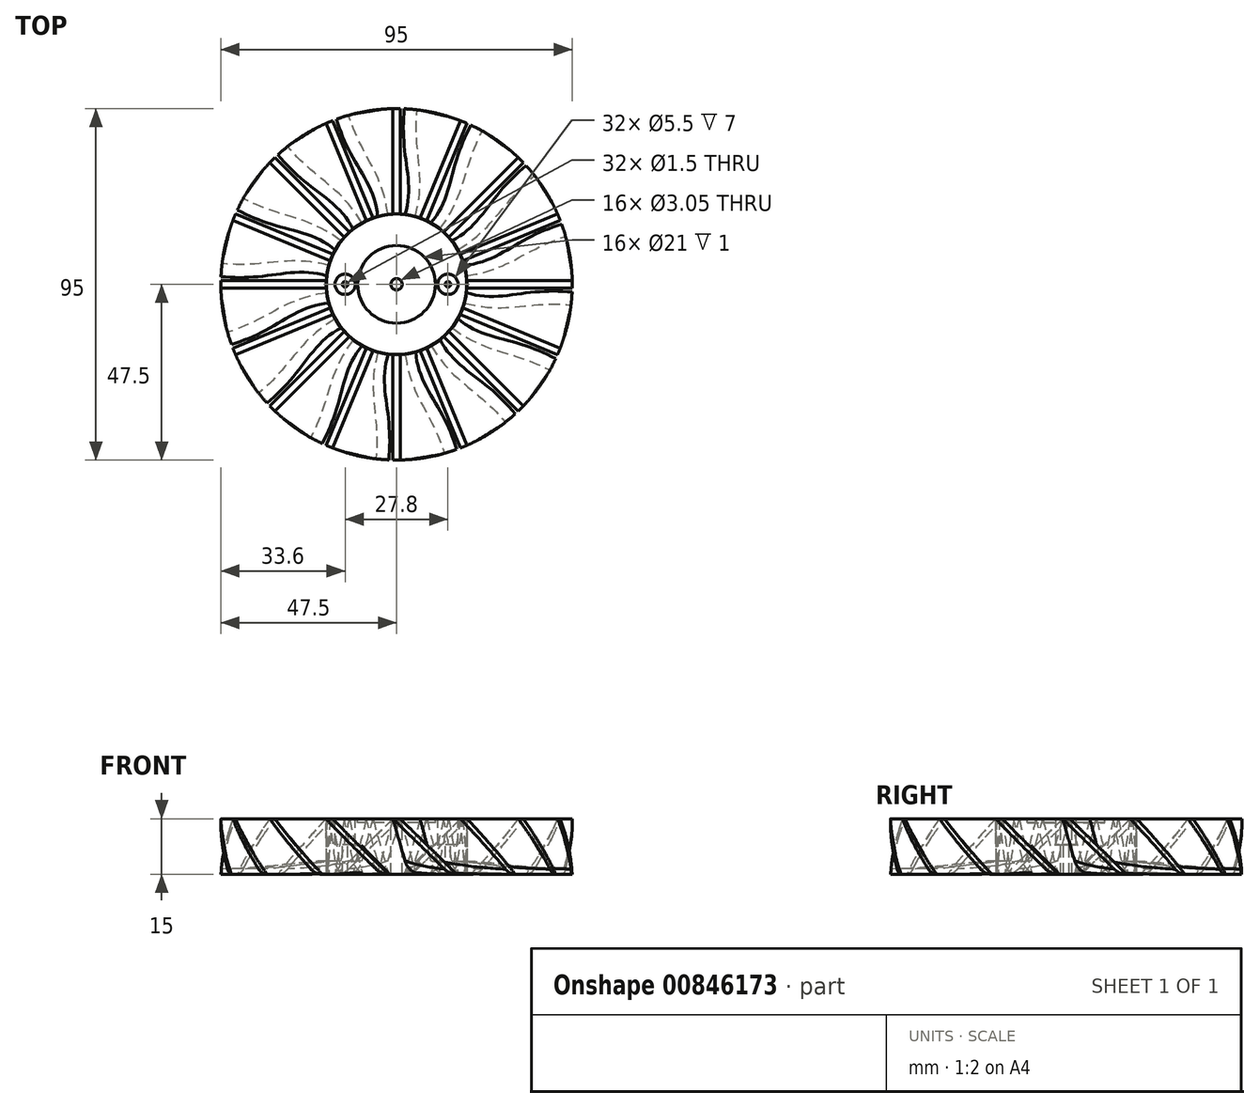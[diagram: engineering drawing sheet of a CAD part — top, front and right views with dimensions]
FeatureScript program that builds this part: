
annotation { "Feature Type Name" : "Feature", "Feature Type Description" : "" }
export const myFeature = defineFeature(function(context is Context, id is Id, definition is map)
    precondition{}
    {
        {
            var Q0;
            Q0=qCreatedBy(makeId("Top.planeOp"),FACE);
            var sketch = newSketch(context, id + "F0", { "sketchPlane" : qUnion([Q0])});
            skCircle(sketch, "E0", {"center": v(0, 0) * mm, "radius": 19 * mm});
            skSolve(sketch);
        }
        {
            var Q0;
            Q0=qSketchRegion(id+"F0",true);
            extrude(context, id + "F1", {"entities" : qUnion([Q0]), "depth" : 15 * mm, "offsetDistance" : 25 * mm});
        }
        {
            var Q0;
            Q0=makeQuery(id+"F1.opExtrude","CAP_FACE",FACE,{"disambiguationData":[OSD([sQuery(id+"F0.wireOp",EDGE,"E0")])],"isStart":true});
            var sketch = newSketch(context, id + "F2", { "sketchPlane" : qUnion([Q0])});
            skLineSegment(sketch, "E1", {"start": v(0, 0) * mm, "end": v(-3.3, -18.71) * mm});
            skLineSegment(sketch, "E2", {"start": v(0, 0) * mm, "end": v(0, -19) * mm, "construction": true});
            skCircle(sketch, "E3", {"center": v(0, 0) * mm, "radius": 49 * mm, "construction": true});
            skFitSpline(sketch, "E4", {"points": [v(-3.3, -18.71) * mm, v(-14.76, -46.73) * mm], "startDerivative": vector(-6.25, -35.44) * mm, "endDerivative": vector(-12.11, -41.2) * mm});
            skFitSpline(sketch, "E5.0", {"points": [v(-5.27, -18.36) * mm, v(-5.52, -19.77) * mm, v(-6.1, -22.3) * mm, v(-7.22, -25.45) * mm, v(-8.53, -28.26) * mm, v(-10.02, -31) * mm, v(-11.66, -33.93) * mm, v(-13.37, -37.26) * mm, v(-15.07, -41.21) * mm, v(-16.15, -44.4) * mm, v(-16.67, -46.16) * mm]});
            skLineSegment(sketch, "E5.1", {"start": v(-1.97, 0.35) * mm, "end": v(-5.27, -18.36) * mm});
            skLineSegment(sketch, "E6", {"start": v(-14.76, -46.73) * mm, "end": v(-16.67, -46.16) * mm});
            skLineSegment(sketch, "E7", {"start": v(-3.3, -18.71) * mm, "end": v(-4.64, -17.92) * mm});
            skLineSegment(sketch, "E8", {"start": v(-4.64, -17.92) * mm, "end": v(-5.2, -17.92) * mm});
            skLineSegment(sketch, "E9", {"start": v(-5.2, -17.92) * mm, "end": v(-5.27, -18.36) * mm});
            skSolve(sketch);
        }
        {
            var Q0;
            Q0=makeQuery(id+"F1.opExtrude","CAP_FACE",FACE,{"disambiguationData":[OSD([sQuery(id+"F0.wireOp",EDGE,"E0")])],"isStart":false});
            var sketch = newSketch(context, id + "F3", { "sketchPlane" : qUnion([Q0])});
            skLineSegment(sketch, "E10", {"start": v(-0.97, 18.98) * mm, "end": v(0.97, 18.98) * mm});
            skLineSegment(sketch, "E11", {"start": v(0.97, 18.98) * mm, "end": v(0.97, 49) * mm});
            skLineSegment(sketch, "E12", {"start": v(0.97, 49) * mm, "end": v(-0.97, 49) * mm});
            skLineSegment(sketch, "E13", {"start": v(-0.97, 49) * mm, "end": v(-0.97, 18.98) * mm});
            skSolve(sketch);
        }
        {
            var Q1;
            {var subQ4=sQuery(id+"F2.wireOp",EDGE,"E4");Q1=makeQuery(id+"F2.imprint","IMPRINT",FACE,{"disambiguationData":[TD([[makeQuery(id+"F2.imprint","IMPRINT",EDGE,{"derivedFrom":subQ4}),-1.0]])]});}
            var Q2;
            {var subQ0=sQuery(id+"F3.wireOp",EDGE,"E11");Q2=makeQuery(id+"F3.imprint","IMPRINT",FACE,{"disambiguationData":[TD([[makeQuery(id+"F3.imprint","IMPRINT",EDGE,{"derivedFrom":subQ0}),1.0]])]});}
            var Q3;
            Q3=sQuery(id+"F2.wireOp",VERTEX,"E6.end");
            var Q4;
            Q4=sQuery(id+"F3.wireOp",VERTEX,"E13.start");
            loft(context, id + "F4", {"operationType" : NewBodyOperationType.ADD, "sheetProfilesArray" : [{ "sheetProfileEntities" : qUnion([Q1]) }, { "sheetProfileEntities" : qUnion([Q2]) }], "matchConnections" : true, "connections" : [{ "connectionEntities" : qUnion([Q3, Q4]), "connectionEdgeQueries" : qUnion([]), "connectionEdgeParameters" : [] }]});
        }
        {
            var Q0;
            Q0=makeQuery(id+"F4.opLoft","SWEPT_EDGE",EDGE,{"disambiguationData":[OSD([sQuery(id+"F2.wireOp",EDGE,"E4"),sQuery(id+"F2.wireOp",EDGE,"E6"),sQuery(id+"F3.wireOp",EDGE,"E11"),sQuery(id+"F3.wireOp",EDGE,"E12")])]});
            var Q1;
            Q1=makeQuery(id+"F4.opLoft","SWEPT_EDGE",EDGE,{"disambiguationData":[OSD([sQuery(id+"F2.wireOp",EDGE,"E5.0"),sQuery(id+"F2.wireOp",EDGE,"E6"),sQuery(id+"F3.wireOp",EDGE,"E12"),sQuery(id+"F3.wireOp",EDGE,"E13")])]});
            fillet(context, id + "F5", {"entities" : qUnion([Q0, Q1]), "radius" : 1 * mm, "tangentPropagation" : true, "allowEdgeOverflow" : false});
        }
        {
            var Q0;
            Q0=qCreatedBy(makeId("Right.planeOp"),FACE);
            var sketch = newSketch(context, id + "F6", { "sketchPlane" : qUnion([Q0])});
            skLineSegment(sketch, "E14", {"start": v(0, -43.46) * mm, "end": v(0, 53.88) * mm, "construction": true});
            skSolve(sketch);
        }
        {
            var Q0;
            Q0=makeQuery(id+"F1.opExtrude","SWEPT_BODY",BODY,{"disambiguationData":[OSD([sQuery(id+"F0.wireOp",EDGE,"E0")])]});
            var Q1;
            Q1=sQuery(id+"F6.wireOp",EDGE,"E14");
            circularPattern(context, id + "F7", {"entities" : qUnion([Q0]), "axis" : qUnion([Q1]), "angle" : 360 * degree, "instanceCount" : 16, "equalSpace" : true});
        }
        {
            var Q0;
            {var subQ0=sQuery(id+"F3.wireOp",EDGE,"E11");var subQ3=sQuery(id+"F0.wireOp",EDGE,"E0");Q0=makeQuery(id+"F7.opPattern","COPY",FACE,{"derivedFrom":makeQuery(id+"F4.boolean.opBoolean","MERGE",FACE,{"derivedFrom":[makeQuery(id+"F1.opExtrude","CAP_FACE",FACE,{"disambiguationData":[OSD([subQ3])],"isStart":false}),makeQuery(id+"F4.opLoft","CAP_FACE",FACE,{"disambiguationData":[OSD([makeQuery(id+"F3.imprint","IMPRINT",FACE,{"disambiguationData":[TD([[makeQuery(id+"F3.imprint","IMPRINT",EDGE,{"derivedFrom":subQ0}),1.0]])]})])],"isStart":true})]}),"instanceName":"2"});}
            var sketch = newSketch(context, id + "F8", { "sketchPlane" : qUnion([Q0])});
            skCircle(sketch, "E15", {"center": v(0, 0) * mm, "radius": 47.5 * mm});
            skCircle(sketch, "E16", {"center": v(0, 0) * mm, "radius": 52.62 * mm});
            skSolve(sketch);
        }
        {
            var Q0;
            Q0=qSketchRegion(id+"F8",true);
            extrude(context, id + "F9", {"entities" : qUnion([Q0]), "operationType" : NewBodyOperationType.REMOVE, "endBound" : BoundingType.THROUGH_ALL, "oppositeDirection" : true, "depth" : 15 * mm, "offsetDistance" : 25 * mm});
        }
        {
            var Q0;
            {var subQ0=sQuery(id+"F3.wireOp",EDGE,"E11");var subQ3=sQuery(id+"F0.wireOp",EDGE,"E0");Q0=makeQuery(id+"F7.opPattern","COPY",FACE,{"derivedFrom":makeQuery(id+"F4.boolean.opBoolean","MERGE",FACE,{"derivedFrom":[makeQuery(id+"F1.opExtrude","CAP_FACE",FACE,{"disambiguationData":[OSD([subQ3])],"isStart":false}),makeQuery(id+"F4.opLoft","CAP_FACE",FACE,{"disambiguationData":[OSD([makeQuery(id+"F3.imprint","IMPRINT",FACE,{"disambiguationData":[TD([[makeQuery(id+"F3.imprint","IMPRINT",EDGE,{"derivedFrom":subQ0}),1.0]])]})])],"isStart":true})]}),"instanceName":"11"});}
            var sketch = newSketch(context, id + "F10", { "sketchPlane" : qUnion([Q0])});
            skCircle(sketch, "E17", {"center": v(0, 0) * mm, "radius": 1.52 * mm});
            skSolve(sketch);
        }
        {
            var Q0;
            Q0=qSketchRegion(id+"F10",true);
            extrude(context, id + "F11", {"entities" : qUnion([Q0]), "operationType" : NewBodyOperationType.REMOVE, "endBound" : BoundingType.THROUGH_ALL, "oppositeDirection" : true, "depth" : 25 * mm, "offsetDistance" : 25 * mm});
        }
        {
            var Q0;
            {var subQ0=sQuery(id+"F3.wireOp",EDGE,"E11");var subQ3=sQuery(id+"F0.wireOp",EDGE,"E0");Q0=makeQuery(id+"F7.opPattern","COPY",FACE,{"derivedFrom":makeQuery(id+"F4.boolean.opBoolean","MERGE",FACE,{"derivedFrom":[makeQuery(id+"F1.opExtrude","CAP_FACE",FACE,{"disambiguationData":[OSD([subQ3])],"isStart":false}),makeQuery(id+"F4.opLoft","CAP_FACE",FACE,{"disambiguationData":[OSD([makeQuery(id+"F3.imprint","IMPRINT",FACE,{"disambiguationData":[TD([[makeQuery(id+"F3.imprint","IMPRINT",EDGE,{"derivedFrom":subQ0}),1.0]])]})])],"isStart":true})]}),"instanceName":"8"});}
            var sketch = newSketch(context, id + "F12", { "sketchPlane" : qUnion([Q0])});
            skLineSegment(sketch, "E18", {"start": v(0, 0) * mm, "end": v(14.1, 0) * mm, "construction": true});
            skLineSegment(sketch, "E19", {"start": v(14.1, 0) * mm, "end": v(-16.8, 0) * mm, "construction": true});
            skCircle(sketch, "E20", {"center": v(-13.9, 0) * mm, "radius": 2.75 * mm});
            skCircle(sketch, "E21", {"center": v(13.9, 0) * mm, "radius": 2.75 * mm});
            skPoint(sketch, "E22", {"position": v(-11.15, 0) * mm});
            skPoint(sketch, "E23", {"position": v(11.15, 0) * mm});
            skCircle(sketch, "E24", {"center": v(0, 0) * mm, "radius": 10.5 * mm});
            skSolve(sketch);
        }
        {
            var Q0;
            Q0=makeQuery(id+"F12.imprint","IMPRINT",FACE,{"disambiguationData":[TD([[makeQuery(id+"F12.imprint","IMPRINT",EDGE,{"derivedFrom":sQuery(id+"F12.wireOp",EDGE,"E24")}),1.0]])]});
            extrude(context, id + "F13", {"entities" : qUnion([Q0]), "operationType" : NewBodyOperationType.REMOVE, "oppositeDirection" : true, "depth" : 1 * mm, "offsetDistance" : 25 * mm});
        }
        {
            var Q0;
            Q0=makeQuery(id+"F12.imprint","IMPRINT",FACE,{"disambiguationData":[TD([[makeQuery(id+"F12.imprint","IMPRINT",EDGE,{"derivedFrom":sQuery(id+"F12.wireOp",EDGE,"E20")}),1.0]])]});
            var Q1;
            Q1=makeQuery(id+"F12.imprint","IMPRINT",FACE,{"disambiguationData":[TD([[makeQuery(id+"F12.imprint","IMPRINT",EDGE,{"derivedFrom":sQuery(id+"F12.wireOp",EDGE,"E21")}),1.0]])]});
            extrude(context, id + "F14", {"entities" : qUnion([Q0, Q1]), "operationType" : NewBodyOperationType.REMOVE, "oppositeDirection" : true, "depth" : 7 * mm, "offsetDistance" : 25 * mm});
        }
        {
            var Q0;
            Q0=makeQuery(id+"F14.boolean.opBoolean","COPY",FACE,{"disambiguationData":[OD(2.0)],"derivedFrom":makeQuery(id+"F14.opExtrude","CAP_FACE",FACE,{"disambiguationData":[OSD([sQuery(id+"F12.wireOp",EDGE,"E20")])],"isStart":false})});
            var sketch = newSketch(context, id + "F15", { "sketchPlane" : qUnion([Q0])});
            skCircle(sketch, "E25", {"center": v(-13.9, 0) * mm, "radius": 0.75 * mm});
            skSolve(sketch);
        }
        {
            var Q0;
            Q0=qSketchRegion(id+"F15",true);
            extrude(context, id + "F16", {"entities" : qUnion([Q0]), "operationType" : NewBodyOperationType.REMOVE, "oppositeDirection" : true, "depth" : 25 * mm, "offsetDistance" : 25 * mm});
        }
        {
            var Q0;
            Q0=makeQuery(id+"F14.boolean.opBoolean","COPY",FACE,{"disambiguationData":[OD(2.0)],"derivedFrom":makeQuery(id+"F14.opExtrude","CAP_FACE",FACE,{"disambiguationData":[OSD([sQuery(id+"F12.wireOp",EDGE,"E21")])],"isStart":false})});
            var sketch = newSketch(context, id + "F17", { "sketchPlane" : qUnion([Q0])});
            skCircle(sketch, "E26", {"center": v(13.9, 0) * mm, "radius": 0.75 * mm});
            skSolve(sketch);
        }
        {
            var Q0;
            Q0=qSketchRegion(id+"F17",true);
            extrude(context, id + "F18", {"entities" : qUnion([Q0]), "operationType" : NewBodyOperationType.REMOVE, "oppositeDirection" : true, "depth" : 25 * mm, "offsetDistance" : 25 * mm});
        }
        {
            var Q0;
            Q0=makeQuery(id+"F7.opPattern","COPY",EDGE,{"derivedFrom":makeQuery(id+"F4.opLoft","MID_CAP_EDGE",EDGE,{"disambiguationData":[OSD([sQuery(id+"F0.wireOp",EDGE,"E0"),sQuery(id+"F2.wireOp",EDGE,"E4"),sQuery(id+"F2.wireOp",EDGE,"E6"),sQuery(id+"F2.wireOp",EDGE,"E7")])],"capPos":0.0}),"instanceName":"10"});
            var Q1;
            Q1=makeQuery(id+"F7.opPattern","COPY",EDGE,{"derivedFrom":makeQuery(id+"F4.opLoft","MID_CAP_EDGE",EDGE,{"disambiguationData":[OSD([sQuery(id+"F0.wireOp",EDGE,"E0"),sQuery(id+"F2.wireOp",EDGE,"E4"),sQuery(id+"F2.wireOp",EDGE,"E6"),sQuery(id+"F2.wireOp",EDGE,"E7")])],"capPos":0.0}),"instanceName":"11"});
            var Q2;
            Q2=makeQuery(id+"F7.opPattern","COPY",EDGE,{"derivedFrom":makeQuery(id+"F4.opLoft","MID_CAP_EDGE",EDGE,{"disambiguationData":[OSD([sQuery(id+"F0.wireOp",EDGE,"E0"),sQuery(id+"F2.wireOp",EDGE,"E4"),sQuery(id+"F2.wireOp",EDGE,"E6"),sQuery(id+"F2.wireOp",EDGE,"E7")])],"capPos":0.0}),"instanceName":"12"});
            var Q3;
            Q3=makeQuery(id+"F7.opPattern","COPY",EDGE,{"derivedFrom":makeQuery(id+"F4.opLoft","MID_CAP_EDGE",EDGE,{"disambiguationData":[OSD([sQuery(id+"F0.wireOp",EDGE,"E0"),sQuery(id+"F2.wireOp",EDGE,"E4"),sQuery(id+"F2.wireOp",EDGE,"E6"),sQuery(id+"F2.wireOp",EDGE,"E7")])],"capPos":0.0}),"instanceName":"13"});
            var Q4;
            Q4=makeQuery(id+"F7.opPattern","COPY",EDGE,{"derivedFrom":makeQuery(id+"F4.opLoft","MID_CAP_EDGE",EDGE,{"disambiguationData":[OSD([sQuery(id+"F0.wireOp",EDGE,"E0"),sQuery(id+"F2.wireOp",EDGE,"E4"),sQuery(id+"F2.wireOp",EDGE,"E6"),sQuery(id+"F2.wireOp",EDGE,"E7")])],"capPos":0.0}),"instanceName":"14"});
            var Q5;
            Q5=makeQuery(id+"F7.opPattern","COPY",EDGE,{"derivedFrom":makeQuery(id+"F4.opLoft","MID_CAP_EDGE",EDGE,{"disambiguationData":[OSD([sQuery(id+"F0.wireOp",EDGE,"E0"),sQuery(id+"F2.wireOp",EDGE,"E4"),sQuery(id+"F2.wireOp",EDGE,"E6"),sQuery(id+"F2.wireOp",EDGE,"E7")])],"capPos":0.0}),"instanceName":"15"});
            var Q6;
            Q6=makeQuery(id+"F4.opLoft","MID_CAP_EDGE",EDGE,{"disambiguationData":[OSD([sQuery(id+"F0.wireOp",EDGE,"E0"),sQuery(id+"F2.wireOp",EDGE,"E4"),sQuery(id+"F2.wireOp",EDGE,"E6"),sQuery(id+"F2.wireOp",EDGE,"E7")])],"capPos":0.0});
            var Q7;
            Q7=makeQuery(id+"F7.opPattern","COPY",EDGE,{"derivedFrom":makeQuery(id+"F4.opLoft","MID_CAP_EDGE",EDGE,{"disambiguationData":[OSD([sQuery(id+"F0.wireOp",EDGE,"E0"),sQuery(id+"F2.wireOp",EDGE,"E4"),sQuery(id+"F2.wireOp",EDGE,"E6"),sQuery(id+"F2.wireOp",EDGE,"E7")])],"capPos":0.0}),"instanceName":"1"});
            var Q8;
            Q8=makeQuery(id+"F7.opPattern","COPY",EDGE,{"derivedFrom":makeQuery(id+"F4.opLoft","MID_CAP_EDGE",EDGE,{"disambiguationData":[OSD([sQuery(id+"F0.wireOp",EDGE,"E0"),sQuery(id+"F2.wireOp",EDGE,"E4"),sQuery(id+"F2.wireOp",EDGE,"E6"),sQuery(id+"F2.wireOp",EDGE,"E7")])],"capPos":0.0}),"instanceName":"2"});
            var Q9;
            Q9=makeQuery(id+"F7.opPattern","COPY",EDGE,{"derivedFrom":makeQuery(id+"F4.opLoft","MID_CAP_EDGE",EDGE,{"disambiguationData":[OSD([sQuery(id+"F0.wireOp",EDGE,"E0"),sQuery(id+"F2.wireOp",EDGE,"E4"),sQuery(id+"F2.wireOp",EDGE,"E6"),sQuery(id+"F2.wireOp",EDGE,"E7")])],"capPos":0.0}),"instanceName":"3"});
            var Q10;
            Q10=makeQuery(id+"F7.opPattern","COPY",EDGE,{"derivedFrom":makeQuery(id+"F4.opLoft","MID_CAP_EDGE",EDGE,{"disambiguationData":[OSD([sQuery(id+"F0.wireOp",EDGE,"E0"),sQuery(id+"F2.wireOp",EDGE,"E4"),sQuery(id+"F2.wireOp",EDGE,"E6"),sQuery(id+"F2.wireOp",EDGE,"E7")])],"capPos":0.0}),"instanceName":"4"});
            var Q11;
            Q11=makeQuery(id+"F7.opPattern","COPY",EDGE,{"derivedFrom":makeQuery(id+"F4.opLoft","MID_CAP_EDGE",EDGE,{"disambiguationData":[OSD([sQuery(id+"F0.wireOp",EDGE,"E0"),sQuery(id+"F2.wireOp",EDGE,"E4"),sQuery(id+"F2.wireOp",EDGE,"E6"),sQuery(id+"F2.wireOp",EDGE,"E7")])],"capPos":0.0}),"instanceName":"5"});
            var Q12;
            Q12=makeQuery(id+"F7.opPattern","COPY",EDGE,{"derivedFrom":makeQuery(id+"F4.opLoft","MID_CAP_EDGE",EDGE,{"disambiguationData":[OSD([sQuery(id+"F0.wireOp",EDGE,"E0"),sQuery(id+"F2.wireOp",EDGE,"E4"),sQuery(id+"F2.wireOp",EDGE,"E6"),sQuery(id+"F2.wireOp",EDGE,"E7")])],"capPos":0.0}),"instanceName":"6"});
            var Q13;
            Q13=makeQuery(id+"F7.opPattern","COPY",EDGE,{"derivedFrom":makeQuery(id+"F4.opLoft","MID_CAP_EDGE",EDGE,{"disambiguationData":[OSD([sQuery(id+"F0.wireOp",EDGE,"E0"),sQuery(id+"F2.wireOp",EDGE,"E4"),sQuery(id+"F2.wireOp",EDGE,"E6"),sQuery(id+"F2.wireOp",EDGE,"E7")])],"capPos":0.0}),"instanceName":"7"});
            var Q14;
            Q14=makeQuery(id+"F7.opPattern","COPY",EDGE,{"derivedFrom":makeQuery(id+"F4.opLoft","MID_CAP_EDGE",EDGE,{"disambiguationData":[OSD([sQuery(id+"F0.wireOp",EDGE,"E0"),sQuery(id+"F2.wireOp",EDGE,"E4"),sQuery(id+"F2.wireOp",EDGE,"E6"),sQuery(id+"F2.wireOp",EDGE,"E7")])],"capPos":0.0}),"instanceName":"8"});
            var Q15;
            Q15=makeQuery(id+"F7.opPattern","COPY",EDGE,{"derivedFrom":makeQuery(id+"F4.opLoft","MID_CAP_EDGE",EDGE,{"disambiguationData":[OSD([sQuery(id+"F0.wireOp",EDGE,"E0"),sQuery(id+"F2.wireOp",EDGE,"E4"),sQuery(id+"F2.wireOp",EDGE,"E6"),sQuery(id+"F2.wireOp",EDGE,"E7")])],"capPos":0.0}),"instanceName":"9"});
            fillet(context, id + "F19", {"entities" : qUnion([Q0, Q1, Q2, Q3, Q4, Q5, Q6, Q7, Q8, Q9, Q10, Q11, Q12, Q13, Q14, Q15]), "radius" : 5 * mm, "tangentPropagation" : true, "allowEdgeOverflow" : false});
        }
    });
